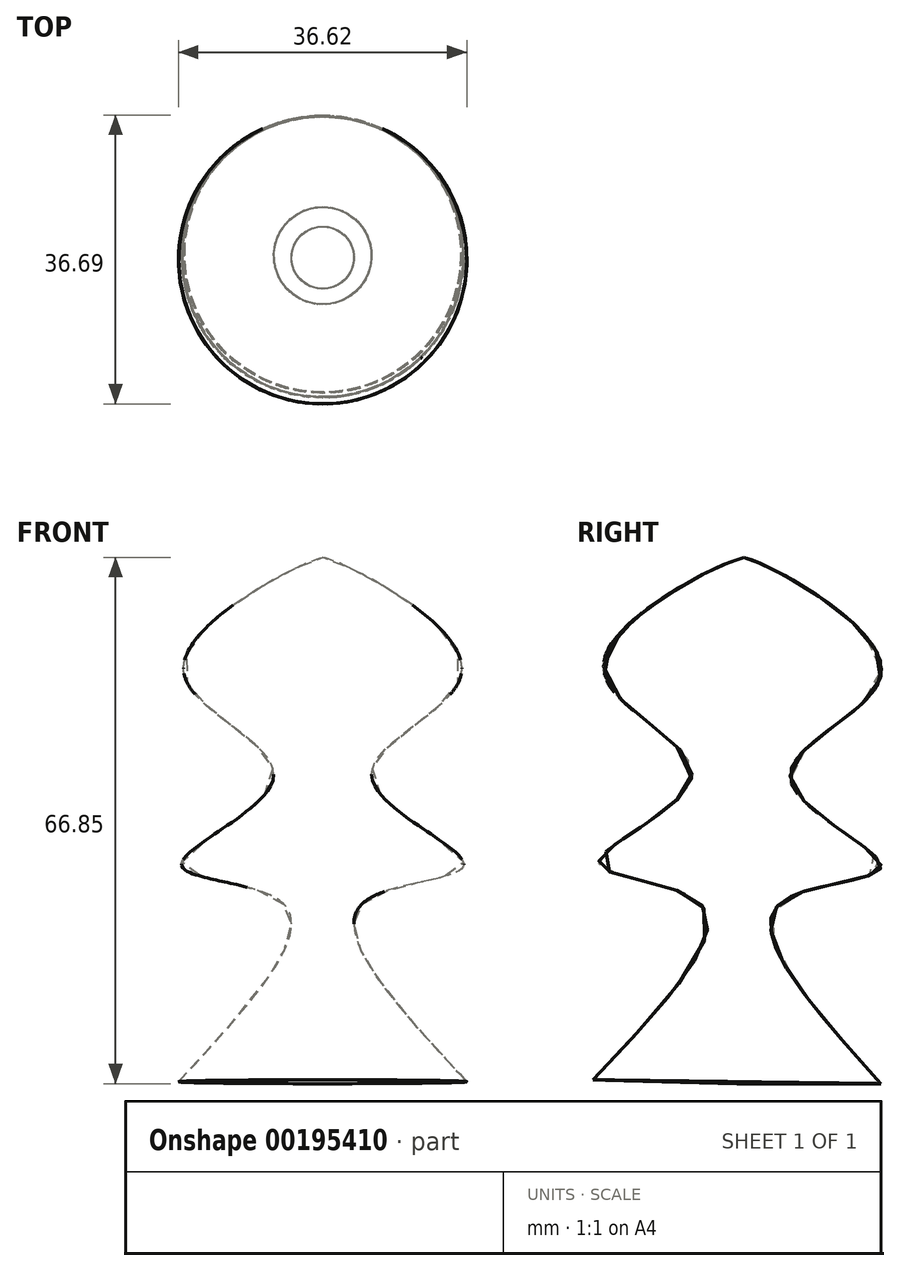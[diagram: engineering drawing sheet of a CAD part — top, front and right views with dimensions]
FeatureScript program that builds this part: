
annotation { "Feature Type Name" : "Feature", "Feature Type Description" : "" }
export const myFeature = defineFeature(function(context is Context, id is Id, definition is map)
    precondition{}
    {
        {
            var Q0;
            Q0=qCreatedBy(makeId("Right.planeOp"),FACE);
            var sketch = newSketch(context, id + "F0", { "sketchPlane" : qUnion([Q0])});
            skLineSegment(sketch, "E0", {"start": v(0, 0) * mm, "end": v(18.31, 0) * mm});
            skFitSpline(sketch, "E1", {"points": [v(18.31, 0) * mm, v(5.35, 22.82) * mm, v(18.31, 27.6) * mm, v(6.76, 38.88) * mm, v(18.31, 51.84) * mm, v(3.94, 65.64) * mm, v(0, 67.05) * mm], "startDerivative": vector(-118.34, 130.44) * mm, "endDerivative": vector(-30.91, 6.3) * mm});
            skLineSegment(sketch, "E2", {"start": v(0.9, 66.87) * mm, "end": v(0, 0) * mm});
            skSolve(sketch);
        }
        {
            var Q0;
            {var subQ0=sQuery(id+"F0.wireOp",EDGE,"E0");Q0=makeQuery(id+"F0.imprint","IMPRINT",FACE,{"disambiguationData":[TD([[makeQuery(id+"F0.imprint","IMPRINT",EDGE,{"derivedFrom":subQ0}),1.0]])]});}
            var Q1;
            Q1=sQuery(id+"F0.wireOp",EDGE,"E2");
            revolve(context, id + "F1", {"entities" : qUnion([Q0]), "axis" : qUnion([Q1]), "revolveType" : RevolveType.FULL});
        }
        {
            var Q0;
            Q0=makeQuery(id+"F1.opRevolve","SWEPT_BODY",BODY,{"disambiguationData":[OSD([sQuery(id+"F0.wireOp",EDGE,"E0"),sQuery(id+"F0.wireOp",EDGE,"E1"),sQuery(id+"F0.wireOp",EDGE,"E2")])]});
            var Q1;
            Q1=makeQuery(id+"F1.opRevolve","SWEPT_FACE",FACE,{"disambiguationData":[OSD([sQuery(id+"F0.wireOp",EDGE,"E1")])]});
            circularPattern(context, id + "F2", {"entities" : qUnion([Q0]), "axis" : qUnion([Q1]), "angle" : 360 * degree, "instanceCount" : 8, "equalSpace" : true});
        }
    });
